# Revit family: FT Watex 1LED MODULES_2020
name_source: partatom
category: Lighting Fixtures
units: mm (PartAtom-declared; Revit-internal decimal feet)

## family parameters
Always vertical = Yes
Cut with Voids When Loaded = No
Light Source = Yes
OmniClass Number = 23.80.70.00
OmniClass Title = Lighting
Part Type = Normal
Room Calculation Point = No
Round Connector Dimension = Use Diameter
Shared = No
Work Plane-Based = No

## types (12) — shared parameters
C = 100 mm  [stored 0.328084 ft]
Color Filter = 16777215
D = 110 mm  [stored 0.360892 ft]
Description = https://www.airfal.com
Dimming Lamp Color Temperature Shift = <None>
EX Area = II 3GD Ex nR IIC T5 Gc Ex tb IIIC T100°C Dc
Emergency system = No
Emit from Line Length = 610 mm
IK = IK08
IP = IP66
Led Module = Yes
Tilt Angle = 90.00°
URL = https://www.airfal.com
Useful life = L70B50>50000
zero-valued in all types: Default Elevation

## per-type parameters (varying)
| type | A (Housing) | B | L | L1 (diffuser) | Net output | Photometric Web File | Watts | l (plate) |
| EW113 | 664 mm  [stored 2.17848 ft] | 260 mm  [stored 0.853018 ft] | 600 mm | 660 mm | 1210 lm | EW113 WATEX 600 13W 3000K 1490lm.IES | 13 W | 629 mm |
| EW114 | 664 mm  [stored 2.17848 ft] | 260 mm  [stored 0.853018 ft] | 600 mm | 660 mm | 1259 lm | EW114 WATEX 600 13W 4000K 1550lm.IES | 13 W | 629 mm |
| EW123 | 664 mm  [stored 2.17848 ft] | 260 mm  [stored 0.853018 ft] | 600 mm | 660 mm | 2079 lm | EW123 WATEX 600 16W 3000K 2560lm.IES | 16 W | 629 mm |
| EW124 | 664 mm  [stored 2.17848 ft] | 260 mm  [stored 0.853018 ft] | 600 mm | 660 mm | 2168 lm | EW124 WATEX 600 16W 4000K 2670lm.IES | 16 W | 629 mm |
| EW213 | 1274 mm  [stored 4.17979 ft] | 870 mm  [stored 2.85433 ft] | 1200 mm | 1268 mm | 2420 lm | EW213 WATEX 1200 24W 3000K 2980lm.IES | 24 W | 1274 mm  [stored 4.17979 ft] |
| EW214 | 1274 mm  [stored 4.17979 ft] | 870 mm  [stored 2.85433 ft] | 1200 mm | 1268 mm | 2598 lm | EW214 WATEX 1200 24W 4000K 3200lm.IES | 24 W | 1240 mm  [stored 4.06824 ft] |
| EW223 | 1274 mm  [stored 4.17979 ft] | 870 mm  [stored 2.85433 ft] | 1200 mm | 1268 mm | 4157 lm | EW223 WATEX 1200 32W 3000K 5120lm.IES | 32 W | 1240 mm  [stored 4.06824 ft] |
| EW224 | 1274 mm  [stored 4.17979 ft] | 870 mm  [stored 2.85433 ft] | 1200 mm | 1268 mm | 4336 lm | EW224 WATEX 1200 32W 4000K 5340lm.IES | 32 W | 1240 mm  [stored 4.06824 ft] |
| EW313 | 1575 mm  [stored 5.16732 ft] | 642 mm | 1500 mm  [stored 4.92126 ft] | 1568 mm  [stored 5.14436 ft] | 3021 lm | EW313 WATEX 1500 29W 3000K 3720lm.IES | 29 W | 1541 mm  [stored 5.05577 ft] |
| EW314 | 1575 mm  [stored 5.16732 ft] | 650 mm  [stored 2.13255 ft] | 1500 mm  [stored 4.92126 ft] | 1568 mm  [stored 5.14436 ft] | 3248 lm | EW314 WATEX 1500 29W 4000K 4000lm.IES | 29 W | 1541 mm  [stored 5.05577 ft] |
| EW323 | 1575 mm  [stored 5.16732 ft] | 650 mm  [stored 2.13255 ft] | 1500 mm  [stored 4.92126 ft] | 1568 mm  [stored 5.14436 ft] | 5124 lm | EW323 WATEX 1500 40W 3000K 6310lm.IES | 40 W | 1541 mm  [stored 5.05577 ft] |
| EW324 | 1575 mm  [stored 5.16732 ft] | 650 mm  [stored 2.13255 ft] | 1500 mm  [stored 4.92126 ft] | 1568 mm  [stored 5.14436 ft] | 54404 lm | EW324 WATEX 1500 40W 4000K 6700lm.IES | 40 W | 1541 mm  [stored 5.05577 ft] |

note: [stored X ft] marks values corroborated as IEEE doubles in the binary element streams (Revit-internal decimal feet)

## geometry (parser evidence)
native form markers: Blend x2, Sweep x10
no freeform markers — native parametric forms only
